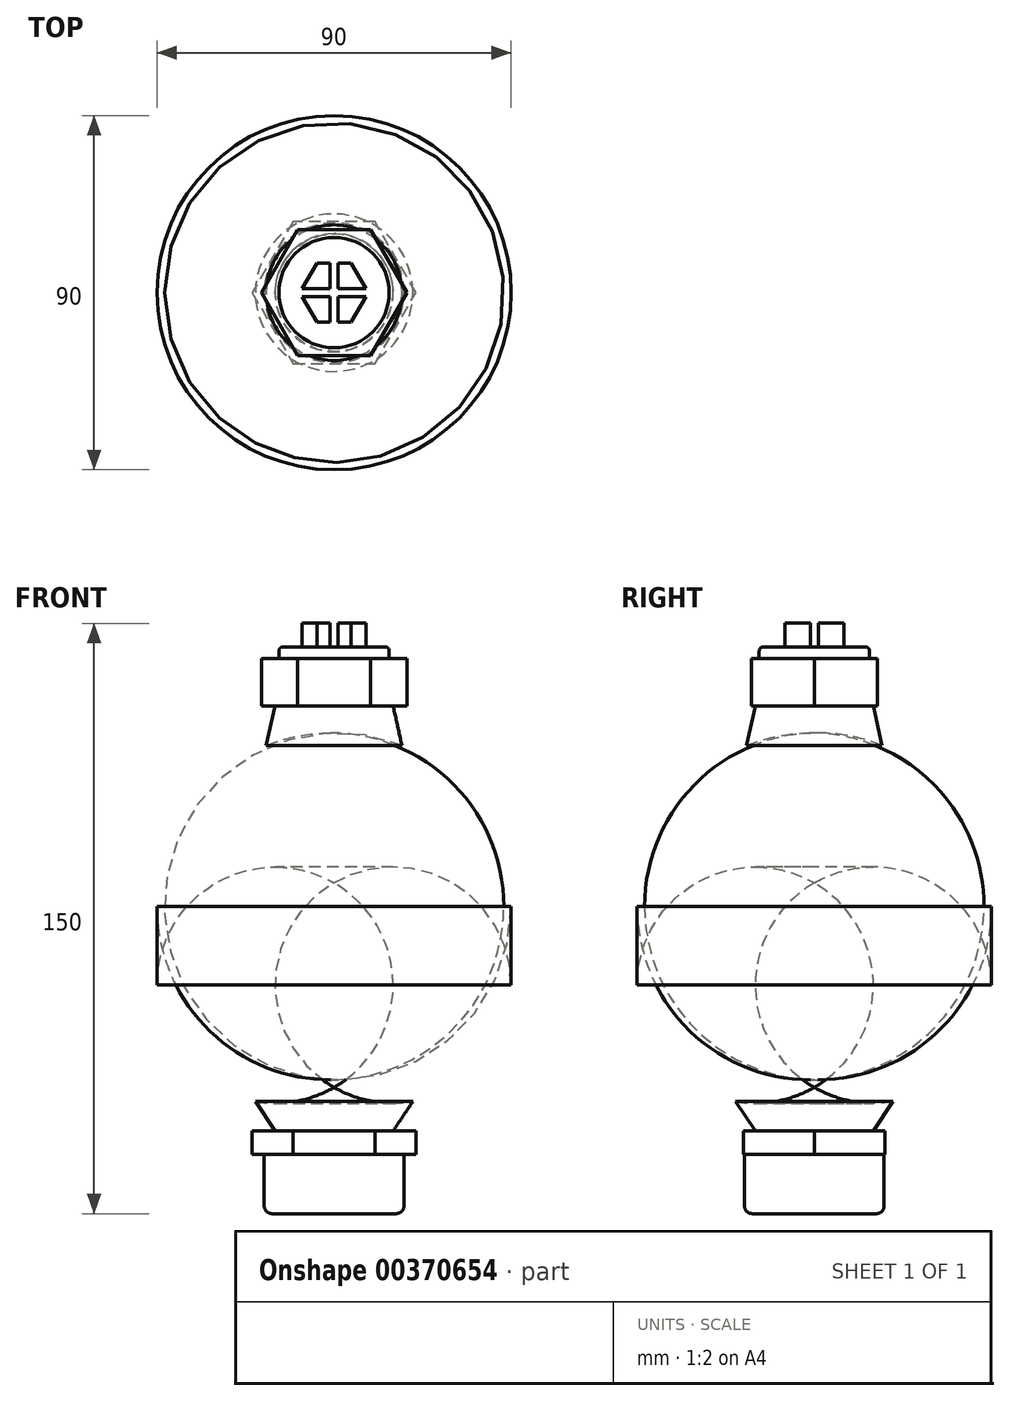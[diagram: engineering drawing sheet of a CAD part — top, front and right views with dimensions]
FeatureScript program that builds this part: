
annotation { "Feature Type Name" : "Feature", "Feature Type Description" : "" }
export const myFeature = defineFeature(function(context is Context, id is Id, definition is map)
    precondition{}
    {
        {
            var Q0;
            Q0=qCreatedBy(makeId("Front.planeOp"),FACE);
            var sketch = newSketch(context, id + "F0", { "sketchPlane" : qUnion([Q0])});
            skLineSegment(sketch, "E0", {"start": v(0, 39.53) * mm, "end": v(0, -68.47) * mm});
            skLineSegment(sketch, "E1", {"start": v(0, 39.53) * mm, "end": v(15, 39.53) * mm});
            skLineSegment(sketch, "E2", {"start": v(0, -68.47) * mm, "end": v(15, -68.47) * mm});
            skLineSegment(sketch, "E3", {"start": v(45, -11.4) * mm, "end": v(45, -31.4) * mm});
            skArc(sketch, "E4", {"start": v(45, -11.4) * mm, "mid": v(37.4, 13.33) * mm, "end": v(17.23, 29.53) * mm});
            skArc(sketch, "E5", {"start": v(45, -31.4) * mm, "mid": v(37.91, -50.77) * mm, "end": v(20, -60.98) * mm});
            skLineSegment(sketch, "E6", {"start": v(15, 39.53) * mm, "end": v(17.23, 29.53) * mm});
            skLineSegment(sketch, "E7", {"start": v(15, -68.47) * mm, "end": v(20, -60.98) * mm});
            skSolve(sketch);
        }
        {
            var Q0;
            Q0=makeQuery(id+"F0.imprint","IMPRINT",FACE,{"disambiguationData":[TD([[makeQuery(id+"F0.imprint","IMPRINT",EDGE,{"derivedFrom":sQuery(id+"F0.wireOp",EDGE,"E0")}),1.0]])]});
            var Q1;
            Q1=sQuery(id+"F0.wireOp",EDGE,"E0");
            revolve(context, id + "F1", {"entities" : qUnion([Q0]), "axis" : qUnion([Q1]), "revolveType" : RevolveType.FULL});
        }
        {
            var Q0;
            Q0=makeQuery(id+"F1.opRevolve","SWEPT_FACE",FACE,{"disambiguationData":[OSD([sQuery(id+"F0.wireOp",EDGE,"E1")])]});
            var sketch = newSketch(context, id + "F2", { "sketchPlane" : qUnion([Q0])});
            skCircle(sketch, "E8.cCircle", {"center": v(0, 0) * mm, "radius": 18.48 * mm, "construction": true});
            skLineSegment(sketch, "E8.0", {"start": v(18.48, 0) * mm, "end": v(9.24, -16) * mm});
            skLineSegment(sketch, "E8.1", {"start": v(9.24, -16) * mm, "end": v(-9.24, -16) * mm});
            skLineSegment(sketch, "E8.2", {"start": v(-9.24, -16) * mm, "end": v(-18.48, 0) * mm});
            skLineSegment(sketch, "E8.3", {"start": v(-18.48, 0) * mm, "end": v(-9.24, 16) * mm});
            skLineSegment(sketch, "E8.4", {"start": v(-9.24, 16) * mm, "end": v(9.24, 16) * mm});
            skLineSegment(sketch, "E8.5", {"start": v(9.24, 16) * mm, "end": v(18.48, 0) * mm});
            skSolve(sketch);
        }
        {
            var Q0;
            Q0 = qSketchRegion(id + "F2", true);
            var Q1;
            Q1=makeQuery(id+"F2.imprint","IMPRINT",FACE,{"disambiguationData":[TD([[makeQuery(id+"F2.imprint","IMPRINT",EDGE,{"derivedFrom":sQuery(id+"F2.wireOp",EDGE,"E8.0")}),-1.0]])]});
            extrude(context, id + "F3", {"entities" : qUnion([Q0, Q1]), "operationType" : NewBodyOperationType.ADD, "depth" : 12 * mm});
        }
        {
            var Q0;
            Q0=makeQuery(id+"F3.opExtrude","CAP_FACE",FACE,{"disambiguationData":[OSD([sQuery(id+"F2.wireOp",EDGE,"E8.0"),sQuery(id+"F2.wireOp",EDGE,"E8.1"),sQuery(id+"F2.wireOp",EDGE,"E8.2"),sQuery(id+"F2.wireOp",EDGE,"E8.3"),sQuery(id+"F2.wireOp",EDGE,"E8.4"),sQuery(id+"F2.wireOp",EDGE,"E8.5")])],"isStart":false});
            var sketch = newSketch(context, id + "F4", { "sketchPlane" : qUnion([Q0])});
            skCircle(sketch, "E9", {"center": v(0, 0) * mm, "radius": 14 * mm});
            skSolve(sketch);
        }
        {
            var Q0;
            Q0=makeQuery(id+"F4.imprint","IMPRINT",FACE,{"disambiguationData":[TD([[makeQuery(id+"F4.imprint","IMPRINT",EDGE,{"derivedFrom":sQuery(id+"F4.wireOp",EDGE,"E9")}),1.0]])]});
            extrude(context, id + "F5", {"entities" : qUnion([Q0]), "operationType" : NewBodyOperationType.ADD, "depth" : 3 * mm});
        }
        {
            var Q0;
            Q0=makeQuery(id+"F5.opExtrude","CAP_EDGE",EDGE,{"disambiguationData":[OSD([sQuery(id+"F4.wireOp",EDGE,"E9")])],"isStart":false});
            fillet(context, id + "F6", {"entities" : qUnion([Q0]), "radius" : 1 * mm, "tangentPropagation" : true, "allowEdgeOverflow" : false});
        }
        {
            var Q0;
            Q0=makeQuery(id+"F5.opExtrude","CAP_FACE",FACE,{"disambiguationData":[OSD([sQuery(id+"F4.wireOp",EDGE,"E9")])],"isStart":false});
            var sketch = newSketch(context, id + "F7", { "sketchPlane" : qUnion([Q0])});
            skCircle(sketch, "E10.cCircle", {"center": v(0, 0) * mm, "radius": 8.66 * mm, "construction": true});
            skLineSegment(sketch, "E10.0", {"start": v(8.66, 0) * mm, "end": v(4.33, -7.5) * mm});
            skLineSegment(sketch, "E10.1", {"start": v(4.33, -7.5) * mm, "end": v(-4.33, -7.5) * mm});
            skLineSegment(sketch, "E10.2", {"start": v(-4.33, -7.5) * mm, "end": v(-8.66, 0) * mm});
            skLineSegment(sketch, "E10.3", {"start": v(-8.66, 0) * mm, "end": v(-4.33, 7.5) * mm});
            skLineSegment(sketch, "E10.4", {"start": v(-4.33, 7.5) * mm, "end": v(4.33, 7.5) * mm});
            skLineSegment(sketch, "E10.5", {"start": v(4.33, 7.5) * mm, "end": v(8.66, 0) * mm});
            skLineSegment(sketch, "E11", {"start": v(-1, 7.5) * mm, "end": v(-1, -7.5) * mm});
            skLineSegment(sketch, "E12", {"start": v(1, -7.5) * mm, "end": v(1, 7.5) * mm});
            skLineSegment(sketch, "E13", {"start": v(-8.08, -1) * mm, "end": v(8.08, -1) * mm});
            skLineSegment(sketch, "E14", {"start": v(-8.08, 1) * mm, "end": v(8.08, 1) * mm});
            skSolve(sketch);
        }
        {
            var Q0;
            {var subQ0=sQuery(id+"F7.wireOp",EDGE,"E10.1");var subQ1=sQuery(id+"F7.wireOp",EDGE,"E10.0");var subQ2=makeQuery(id+"F7.imprint","INTERSECT",VERTEX,{"derivedFrom":[subQ1,subQ0]});Q0=makeQuery(id+"F7.imprint","IMPRINT",FACE,{"disambiguationData":[TD([[makeQuery(id+"F7.imprint","IMPRINT",EDGE,{"disambiguationData":[TD([[subQ2,1.0]])],"derivedFrom":subQ1}),-1.0]])]});}
            var Q1;
            {var subQ0=sQuery(id+"F7.wireOp",EDGE,"E10.2");var subQ1=sQuery(id+"F7.wireOp",EDGE,"E10.1");var subQ2=makeQuery(id+"F7.imprint","INTERSECT",VERTEX,{"derivedFrom":[subQ1,subQ0]});Q1=makeQuery(id+"F7.imprint","IMPRINT",FACE,{"disambiguationData":[TD([[makeQuery(id+"F7.imprint","IMPRINT",EDGE,{"disambiguationData":[TD([[subQ2,1.0]])],"derivedFrom":subQ1}),-1.0]])]});}
            var Q2;
            {var subQ0=sQuery(id+"F7.wireOp",EDGE,"E10.5");var subQ1=sQuery(id+"F7.wireOp",EDGE,"E10.4");var subQ2=makeQuery(id+"F7.imprint","INTERSECT",VERTEX,{"derivedFrom":[subQ1,subQ0]});Q2=makeQuery(id+"F7.imprint","IMPRINT",FACE,{"disambiguationData":[TD([[makeQuery(id+"F7.imprint","IMPRINT",EDGE,{"disambiguationData":[TD([[subQ2,1.0]])],"derivedFrom":subQ1}),-1.0]])]});}
            var Q3;
            {var subQ0=sQuery(id+"F7.wireOp",EDGE,"E10.4");var subQ1=sQuery(id+"F7.wireOp",EDGE,"E10.3");var subQ2=makeQuery(id+"F7.imprint","INTERSECT",VERTEX,{"derivedFrom":[subQ1,subQ0]});Q3=makeQuery(id+"F7.imprint","IMPRINT",FACE,{"disambiguationData":[TD([[makeQuery(id+"F7.imprint","IMPRINT",EDGE,{"disambiguationData":[TD([[subQ2,1.0]])],"derivedFrom":subQ1}),-1.0]])]});}
            extrude(context, id + "F8", {"entities" : qUnion([Q0, Q1, Q2, Q3]), "operationType" : NewBodyOperationType.ADD, "depth" : 6 * mm});
        }
        {
            var Q0;
            Q0=makeQuery(id+"F1.opRevolve","SWEPT_FACE",FACE,{"disambiguationData":[OSD([sQuery(id+"F0.wireOp",EDGE,"E2")])]});
            var sketch = newSketch(context, id + "F9", { "sketchPlane" : qUnion([Q0])});
            skCircle(sketch, "E15.cCircle", {"center": v(0, 0) * mm, "radius": 20.78 * mm, "construction": true});
            skLineSegment(sketch, "E15.0", {"start": v(20.78, 0) * mm, "end": v(10.4, -18) * mm});
            skLineSegment(sketch, "E15.1", {"start": v(10.4, -18) * mm, "end": v(-10.4, -18) * mm});
            skLineSegment(sketch, "E15.2", {"start": v(-10.4, -18) * mm, "end": v(-20.78, 0) * mm});
            skLineSegment(sketch, "E15.3", {"start": v(-20.78, 0) * mm, "end": v(-10.4, 18) * mm});
            skLineSegment(sketch, "E15.4", {"start": v(-10.4, 18) * mm, "end": v(10.4, 18) * mm});
            skLineSegment(sketch, "E15.5", {"start": v(10.4, 18) * mm, "end": v(20.78, 0) * mm});
            skSolve(sketch);
        }
        {
            var Q0;
            Q0 = qSketchRegion(id + "F9", true);
            var Q1;
            Q1=makeQuery(id+"F9.imprint","IMPRINT",FACE,{"disambiguationData":[TD([[makeQuery(id+"F9.imprint","IMPRINT",EDGE,{"derivedFrom":sQuery(id+"F9.wireOp",EDGE,"E15.0")}),-1.0]])]});
            extrude(context, id + "F10", {"entities" : qUnion([Q0, Q1]), "operationType" : NewBodyOperationType.ADD, "depth" : 6 * mm});
        }
        {
            var Q0;
            Q0=makeQuery(id+"F10.opExtrude","CAP_FACE",FACE,{"disambiguationData":[OSD([sQuery(id+"F9.wireOp",EDGE,"E15.0"),sQuery(id+"F9.wireOp",EDGE,"E15.1"),sQuery(id+"F9.wireOp",EDGE,"E15.2"),sQuery(id+"F9.wireOp",EDGE,"E15.3"),sQuery(id+"F9.wireOp",EDGE,"E15.4"),sQuery(id+"F9.wireOp",EDGE,"E15.5")])],"isStart":false});
            var sketch = newSketch(context, id + "F11", { "sketchPlane" : qUnion([Q0])});
            skCircle(sketch, "E16", {"center": v(0, 0) * mm, "radius": 17.75 * mm});
            skSolve(sketch);
        }
        {
            var Q0;
            Q0 = qSketchRegion(id + "F11", true);
            extrude(context, id + "F12", {"entities" : qUnion([Q0]), "operationType" : NewBodyOperationType.ADD, "depth" : 15 * mm});
        }
        {
            var Q0;
            Q0=makeQuery(id+"F12.opExtrude","CAP_EDGE",EDGE,{"disambiguationData":[OSD([sQuery(id+"F11.wireOp",EDGE,"E16")])],"isStart":false});
            fillet(context, id + "F13", {"entities" : qUnion([Q0]), "radius" : 2 * mm, "tangentPropagation" : true, "allowEdgeOverflow" : false});
        }
    });
